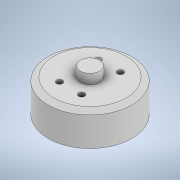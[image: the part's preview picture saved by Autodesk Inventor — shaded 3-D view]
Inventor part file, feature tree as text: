
AUTODESK INVENTOR PART (.ipt)
format: ipt  version: 2020 (Build 240168000, 168)  size: 197,120 bytes
history: native  units: mm
features: sketch x5, extrude x4, projected_geometry x3, chamfer x1, hole x1, pattern_circular x1
ambient origin geometry x8: Origin, YZ Plane, XZ Plane, XY Plane, X Axis, Y Axis, Z Axis, Center Point
bodies: Solid1 (feature_tree)
feature tree (15):
  extrude  "Extrusion1"  Depth=8.5mm TaperAngle=0.0deg
  extrude  "Extrusion2"  Depth=2.6mm TaperAngle=0.0deg
  chamfer  "Chamfer1"  Distance=1.5mm Angle=30.0deg
  extrude  "Extrusion3"  Depth=7.0mm TaperAngle=0.0deg
  hole  "Hole1"  [1 undecoded]
  extrude  "Extrusion4"  Depth=7.0mm
  pattern_circular  "Circular Pattern1"  [2 undecoded]
  sketch  "Sketch1"  dims[d0=22.0mm d1=8.5mm d2=0.0mm]
  sketch  "Sketch2"  dims[d3=5.0mm d4=2.6mm d5=0.0mm d6=1.5mm d7=2.0mm d8=30.0deg]
  sketch  "Sketch3"  dims[d9=20.5mm d10=7.0mm d11=0.0mm]
  sketch  "Sketch4"  dims[d12=5.8mm d13=10.2mm]
  projected_geometry  "Projected Loop1"
  sketch  "Sketch5"  dims[d14=1.6mm d15=6.0mm d16=4.0mm d17=2.0mm d18=90.0deg d19=17.0mm d20=0.0mm d21=0.5mm d22=2.8mm d23=7.0mm d24=0.0mm d25=180.0mm d26=360.0deg]
  projected_geometry  "Projected Loop2"
  projected_geometry  "Projected Loop3"
note: 3 required parameter values undecoded (feature->parameter linkage not recoverable at this tier; creation-order binding heuristic only, values carry confidence <= 0.55)
